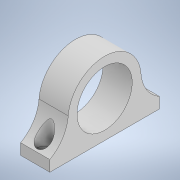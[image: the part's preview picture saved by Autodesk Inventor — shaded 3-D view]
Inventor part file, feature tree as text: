
AUTODESK INVENTOR PART (.ipt)
format: ipt  version: 2020 (Build 240168000, 168)  size: 163,840 bytes
history: native  units: in
note: dims shown in document units (in); Inventor stores cm internally (conversion verified against a paired STEP export)
features: sketch x5, extrude x4, fillet x3, hole x1
ambient origin geometry x8: Origin, YZ Plane, XZ Plane, XY Plane, X Axis, Y Axis, Z Axis, Center Point
bodies: Solid1 (feature_tree)
feature tree (13):
  extrude  "Extrusion1"  Depth=3.0in
  extrude  "Extrusion2"  Depth=0.5in
  extrude  "Extrusion3"  Depth=2.0in
  fillet  "Fillet1"  Radius=1.7in
  sketch  "Sketch4"  dims[d11=1.7in d12=0.0in d13=1.0in]
  fillet  "Fillet2"  Radius=1.0in
  fillet  "Fillet3"  Radius=1.51in
  hole  "Hole1"  [1 undecoded]
  extrude  "Extrusion4"  Depth=0.2in
  sketch  "Sketch1"  dims[d0=0.8in d1=3.0in]
  sketch  "Sketch2"  dims[d2=0.3in d3=0.0in d4=0.5in]
  sketch  "Sketch3"  dims[d5=0.8in d6=2.0in d7=1.7in d8=0.0in d9=1.0in d10=1.51in]
  sketch  "Sketch5"  dims[d14=0.25in d15=0.25in d16=1.0in d17=1.0in d18=0.2in d19=0.75in d20=0.4in d21=0.15in d22=0.5635in d23=1.0in d24=0.8108in d25=0.4in d26=0.4in d27=1.7in d28=0.0in d29=0.5in d30=0.0344in]
note: 1 required parameter value undecoded (feature->parameter linkage not recoverable at this tier; creation-order binding heuristic only, values carry confidence <= 0.55)
